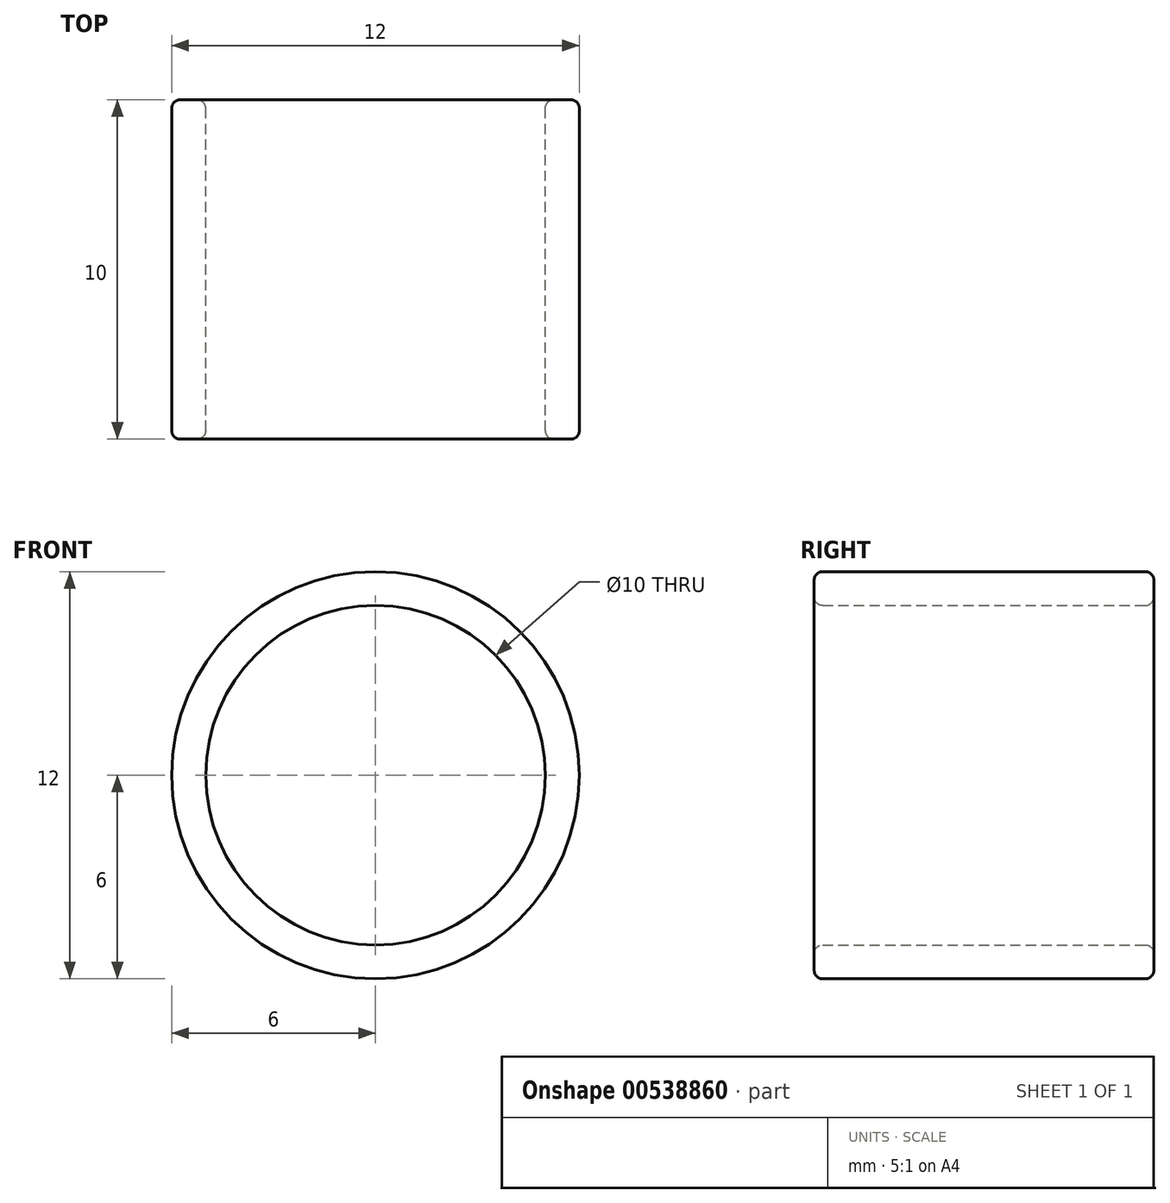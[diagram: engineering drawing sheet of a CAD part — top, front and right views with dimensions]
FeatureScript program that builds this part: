
annotation { "Feature Type Name" : "Feature", "Feature Type Description" : "" }
export const myFeature = defineFeature(function(context is Context, id is Id, definition is map)
    precondition{}
    {
        {
            var Q0;
            Q0=qCreatedBy(makeId("Front.planeOp"),FACE);
            var sketch = newSketch(context, id + "F0", { "sketchPlane" : qUnion([Q0])});
            skCircle(sketch, "E0", {"center": v(0, 0) * mm, "radius": 5 * mm});
            skCircle(sketch, "E1", {"center": v(0, 0) * mm, "radius": 6 * mm});
            skSolve(sketch);
        }
        {
            var Q0;
            Q0 = qSketchRegion(id + "F0", true);
            extrude(context, id + "F1", {"entities" : qUnion([Q0]), "endBound" : BoundingType.SYMMETRIC, "depth" : 10 * mm, "offsetDistance" : 25 * mm});
        }
        {
            var Q0;
            Q0=makeQuery(id+"F1.opExtrude","CAP_FACE",FACE,{"disambiguationData":[OSD([sQuery(id+"F0.wireOp",EDGE,"E0"),sQuery(id+"F0.wireOp",EDGE,"E1")])],"isStart":false});
            var Q1;
            Q1=makeQuery(id+"F1.opExtrude","CAP_FACE",FACE,{"disambiguationData":[OSD([sQuery(id+"F0.wireOp",EDGE,"E0"),sQuery(id+"F0.wireOp",EDGE,"E1")])],"isStart":true});
            fillet(context, id + "F2", {"entities" : qUnion([Q0, Q1]), "radius" : .25 * mm, "tangentPropagation" : true, "allowEdgeOverflow" : false});
        }
    });
